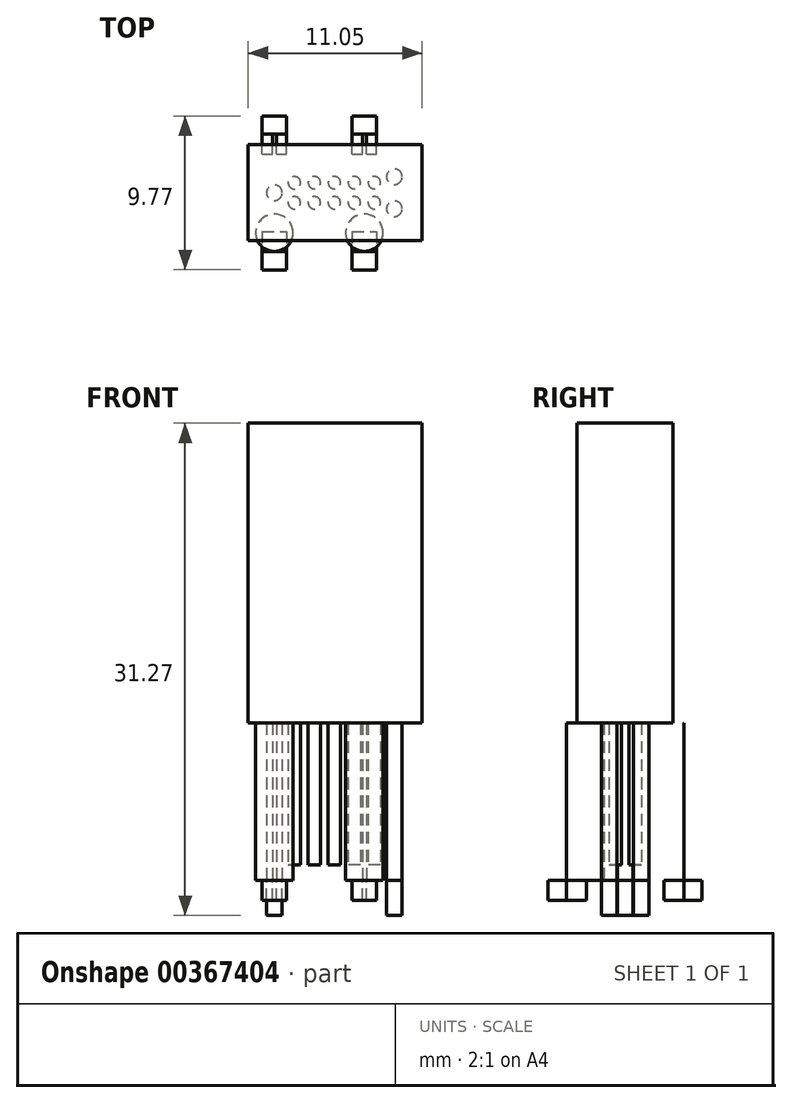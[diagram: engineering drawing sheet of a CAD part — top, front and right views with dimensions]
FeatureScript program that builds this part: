
annotation { "Feature Type Name" : "Feature", "Feature Type Description" : "" }
export const myFeature = defineFeature(function(context is Context, id is Id, definition is map)
    precondition{}
    {
        {
            var Q0;
            Q0=qCreatedBy(makeId("Top.planeOp"),FACE);
            var sketch = newSketch(context, id + "F0", { "sketchPlane" : qUnion([Q0])});
            skCircle(sketch, "E0", {"center": v(0, 0) * mm, "radius": 0.5 * mm});
            skCircle(sketch, "E1", {"center": v(7.62, -1.02) * mm, "radius": 0.5 * mm});
            skCircle(sketch, "E2", {"center": v(7.62, 1.02) * mm, "radius": 0.5 * mm});
            skCircle(sketch, "E3", {"center": v(1.27, 0.64) * mm, "radius": 0.4 * mm});
            skCircle(sketch, "E4", {"center": v(1.27, -0.63) * mm, "radius": 0.4 * mm});
            skCircle(sketch, "E5", {"center": v(2.54, 0.64) * mm, "radius": 0.4 * mm});
            skCircle(sketch, "E6", {"center": v(2.54, -0.63) * mm, "radius": 0.4 * mm});
            skCircle(sketch, "E7", {"center": v(3.81, 0.64) * mm, "radius": 0.4 * mm});
            skCircle(sketch, "E8", {"center": v(3.81, -0.63) * mm, "radius": 0.4 * mm});
            skCircle(sketch, "E9", {"center": v(0, 2.54) * mm, "radius": 1.19 * mm});
            skCircle(sketch, "E10", {"center": v(5.72, 2.54) * mm, "radius": 1.19 * mm});
            skCircle(sketch, "E11", {"center": v(0, -2.54) * mm, "radius": 1.19 * mm});
            skCircle(sketch, "E12", {"center": v(5.72, -2.54) * mm, "radius": 1.19 * mm});
            skLineSegment(sketch, "E13.bottom", {"start": v(-0.77, 4.88) * mm, "end": v(0.77, 4.88) * mm});
            skLineSegment(sketch, "E13.top", {"start": v(-0.77, 3.72) * mm, "end": v(0.77, 3.72) * mm});
            skLineSegment(sketch, "E13.left", {"start": v(-0.77, 4.88) * mm, "end": v(-0.77, 3.72) * mm});
            skLineSegment(sketch, "E13.right", {"start": v(0.77, 4.88) * mm, "end": v(0.77, 3.72) * mm});
            skLineSegment(sketch, "E14.bottom", {"start": v(4.94, 4.88) * mm, "end": v(6.49, 4.88) * mm});
            skLineSegment(sketch, "E14.top", {"start": v(4.94, 3.72) * mm, "end": v(6.49, 3.72) * mm});
            skLineSegment(sketch, "E14.left", {"start": v(4.94, 4.88) * mm, "end": v(4.94, 3.72) * mm});
            skLineSegment(sketch, "E14.right", {"start": v(6.49, 4.88) * mm, "end": v(6.49, 3.72) * mm});
            skLineSegment(sketch, "E15.bottom", {"start": v(-0.77, -3.73) * mm, "end": v(0.77, -3.73) * mm});
            skLineSegment(sketch, "E15.top", {"start": v(-0.77, -4.9) * mm, "end": v(0.77, -4.9) * mm});
            skLineSegment(sketch, "E15.left", {"start": v(-0.77, -3.73) * mm, "end": v(-0.77, -4.9) * mm});
            skLineSegment(sketch, "E15.right", {"start": v(0.77, -3.73) * mm, "end": v(0.77, -4.9) * mm});
            skLineSegment(sketch, "E16.bottom", {"start": v(4.94, -3.73) * mm, "end": v(6.49, -3.73) * mm});
            skLineSegment(sketch, "E16.top", {"start": v(4.94, -4.9) * mm, "end": v(6.49, -4.9) * mm});
            skLineSegment(sketch, "E16.left", {"start": v(4.94, -3.73) * mm, "end": v(4.94, -4.9) * mm});
            skLineSegment(sketch, "E16.right", {"start": v(6.49, -3.73) * mm, "end": v(6.49, -4.9) * mm});
            skCircle(sketch, "E17", {"center": v(5.08, 0.64) * mm, "radius": 0.4 * mm});
            skCircle(sketch, "E18", {"center": v(6.35, 0.64) * mm, "radius": 0.4 * mm});
            skCircle(sketch, "E19", {"center": v(6.35, -0.63) * mm, "radius": 0.4 * mm});
            skCircle(sketch, "E20", {"center": v(5.08, -0.63) * mm, "radius": 0.4 * mm});
            skSolve(sketch);
        }
        {
            var Q0;
            Q0=makeQuery(id+"F0.imprint","IMPRINT",FACE,{"disambiguationData":[TD([[makeQuery(id+"F0.imprint","IMPRINT",EDGE,{"derivedFrom":sQuery(id+"F0.wireOp",EDGE,"E13.bottom")}),-1.0]])]});
            var Q1;
            Q1=makeQuery(id+"F0.imprint","IMPRINT",FACE,{"disambiguationData":[TD([[makeQuery(id+"F0.imprint","IMPRINT",EDGE,{"derivedFrom":sQuery(id+"F0.wireOp",EDGE,"E14.bottom")}),-1.0]])]});
            var Q2;
            Q2=makeQuery(id+"F0.imprint","IMPRINT",FACE,{"disambiguationData":[TD([[makeQuery(id+"F0.imprint","IMPRINT",EDGE,{"derivedFrom":sQuery(id+"F0.wireOp",EDGE,"E15.bottom")}),-1.0]])]});
            var Q3;
            Q3=makeQuery(id+"F0.imprint","IMPRINT",FACE,{"disambiguationData":[TD([[makeQuery(id+"F0.imprint","IMPRINT",EDGE,{"derivedFrom":sQuery(id+"F0.wireOp",EDGE,"E16.bottom")}),-1.0]])]});
            extrude(context, id + "F1", {"entities" : qUnion([Q0, Q1, Q2, Q3]), "depth" : -1.27 * mm});
        }
        {
            var Q0;
            Q0=makeQuery(id+"F0.imprint","IMPRINT",FACE,{"disambiguationData":[TD([[makeQuery(id+"F0.imprint","IMPRINT",EDGE,{"derivedFrom":sQuery(id+"F0.wireOp",EDGE,"E1")}),1.0]])]});
            var Q1;
            Q1=makeQuery(id+"F0.imprint","IMPRINT",FACE,{"disambiguationData":[TD([[makeQuery(id+"F0.imprint","IMPRINT",EDGE,{"derivedFrom":sQuery(id+"F0.wireOp",EDGE,"E2")}),1.0]])]});
            var Q2;
            Q2=makeQuery(id+"F0.imprint","IMPRINT",FACE,{"disambiguationData":[TD([[makeQuery(id+"F0.imprint","IMPRINT",EDGE,{"derivedFrom":sQuery(id+"F0.wireOp",EDGE,"E0")}),1.0]])]});
            extrude(context, id + "F2", {"entities" : qUnion([Q0, Q1, Q2]), "depth" : -2.24 * mm});
        }
        {
            var Q0;
            Q0=makeQuery(id+"F0.imprint","IMPRINT",FACE,{"disambiguationData":[TD([[makeQuery(id+"F0.imprint","IMPRINT",EDGE,{"derivedFrom":sQuery(id+"F0.wireOp",EDGE,"E11")}),1.0]])]});
            var Q1;
            Q1=makeQuery(id+"F0.imprint","IMPRINT",FACE,{"disambiguationData":[TD([[makeQuery(id+"F0.imprint","IMPRINT",EDGE,{"derivedFrom":sQuery(id+"F0.wireOp",EDGE,"E12")}),1.0]])]});
            var Q2;
            {var subQ0=sQuery(id+"F0.wireOp",EDGE,"E14.top");var subQ1=sQuery(id+"F0.wireOp",EDGE,"E10");var subQ2=makeQuery(id+"F0.imprint","INTERSECT",VERTEX,{"disambiguationData":[OD(0.0)],"derivedFrom":[subQ1,subQ0]});Q2=makeQuery(id+"F0.imprint","IMPRINT",FACE,{"disambiguationData":[TD([[makeQuery(id+"F0.imprint","IMPRINT",EDGE,{"disambiguationData":[TD([[subQ2,-1.0]])],"derivedFrom":subQ1}),1.0]])]});}
            var Q3;
            {var subQ0=sQuery(id+"F0.wireOp",EDGE,"E13.top");var subQ1=sQuery(id+"F0.wireOp",EDGE,"E9");var subQ2=makeQuery(id+"F0.imprint","INTERSECT",VERTEX,{"disambiguationData":[OD(0.0)],"derivedFrom":[subQ1,subQ0]});Q3=makeQuery(id+"F0.imprint","IMPRINT",FACE,{"disambiguationData":[TD([[makeQuery(id+"F0.imprint","IMPRINT",EDGE,{"disambiguationData":[TD([[subQ2,-1.0]])],"derivedFrom":subQ1}),1.0]])]});}
            extrude(context, id + "F3", {"entities" : qUnion([Q0, Q1, Q2, Q3]), "depth" : 9.98 * mm});
        }
        {
            var Q0;
            {var subQ0=sQuery(id+"F0.wireOp",EDGE,"E13.top");Q0=makeQuery(id+"F1.opExtrude","SWEPT_FACE",FACE,{"disambiguationData":[OSD([subQ0]),TDD([makeQuery(id+"F0.imprint","IMPRINT",EDGE,{"disambiguationData":[TD([[makeQuery(id+"F0.imprint","INTERSECT",VERTEX,{"derivedFrom":[subQ0,sQuery(id+"F0.wireOp",EDGE,"E13.right")]}),1.0]])],"derivedFrom":subQ0})])]});}
            var Q1;
            {var subQ0=sQuery(id+"F0.wireOp",EDGE,"E13.top");Q1=makeQuery(id+"F1.opExtrude","SWEPT_FACE",FACE,{"disambiguationData":[OSD([subQ0]),TDD([makeQuery(id+"F0.imprint","IMPRINT",EDGE,{"disambiguationData":[TD([[makeQuery(id+"F0.imprint","INTERSECT",VERTEX,{"derivedFrom":[subQ0,sQuery(id+"F0.wireOp",EDGE,"E13.left")]}),-1.0]])],"derivedFrom":subQ0})])]});}
            var Q2;
            {var subQ0=sQuery(id+"F0.wireOp",EDGE,"E14.top");Q2=makeQuery(id+"F1.opExtrude","SWEPT_FACE",FACE,{"disambiguationData":[OSD([subQ0]),TDD([makeQuery(id+"F0.imprint","IMPRINT",EDGE,{"disambiguationData":[TD([[makeQuery(id+"F0.imprint","INTERSECT",VERTEX,{"derivedFrom":[subQ0,sQuery(id+"F0.wireOp",EDGE,"E14.left")]}),-1.0]])],"derivedFrom":subQ0})])]});}
            var Q3;
            {var subQ0=sQuery(id+"F0.wireOp",EDGE,"E14.top");Q3=makeQuery(id+"F1.opExtrude","SWEPT_FACE",FACE,{"disambiguationData":[OSD([subQ0]),TDD([makeQuery(id+"F0.imprint","IMPRINT",EDGE,{"disambiguationData":[TD([[makeQuery(id+"F0.imprint","INTERSECT",VERTEX,{"derivedFrom":[subQ0,sQuery(id+"F0.wireOp",EDGE,"E14.right")]}),1.0]])],"derivedFrom":subQ0})])]});}
            extrude(context, id + "F4", {"entities" : qUnion([Q0, Q1, Q2, Q3]), "depth" : 1.27 * mm});
        }
        {
            var Q0;
            Q0=makeQuery(id+"F1.opExtrude","SWEPT_FACE",FACE,{"disambiguationData":[OSD([sQuery(id+"F0.wireOp",EDGE,"E15.bottom")])]});
            var Q1;
            Q1=makeQuery(id+"F1.opExtrude","SWEPT_FACE",FACE,{"disambiguationData":[OSD([sQuery(id+"F0.wireOp",EDGE,"E16.bottom")])]});
            extrude(context, id + "F5", {"entities" : qUnion([Q0, Q1]), "depth" : 1.27 * mm});
        }
        {
            var Q0;
            Q0=makeQuery(id+"F0.imprint","IMPRINT",FACE,{"disambiguationData":[TD([[makeQuery(id+"F0.imprint","IMPRINT",EDGE,{"derivedFrom":sQuery(id+"F0.wireOp",EDGE,"E8")}),1.0]])]});
            var Q1;
            Q1=makeQuery(id+"F0.imprint","IMPRINT",FACE,{"disambiguationData":[TD([[makeQuery(id+"F0.imprint","IMPRINT",EDGE,{"derivedFrom":sQuery(id+"F0.wireOp",EDGE,"E7")}),1.0]])]});
            var Q2;
            Q2=makeQuery(id+"F0.imprint","IMPRINT",FACE,{"disambiguationData":[TD([[makeQuery(id+"F0.imprint","IMPRINT",EDGE,{"derivedFrom":sQuery(id+"F0.wireOp",EDGE,"E5")}),1.0]])]});
            var Q3;
            Q3=makeQuery(id+"F0.imprint","IMPRINT",FACE,{"disambiguationData":[TD([[makeQuery(id+"F0.imprint","IMPRINT",EDGE,{"derivedFrom":sQuery(id+"F0.wireOp",EDGE,"E6")}),1.0]])]});
            var Q4;
            Q4=makeQuery(id+"F0.imprint","IMPRINT",FACE,{"disambiguationData":[TD([[makeQuery(id+"F0.imprint","IMPRINT",EDGE,{"derivedFrom":sQuery(id+"F0.wireOp",EDGE,"E4")}),1.0]])]});
            var Q5;
            Q5=makeQuery(id+"F0.imprint","IMPRINT",FACE,{"disambiguationData":[TD([[makeQuery(id+"F0.imprint","IMPRINT",EDGE,{"derivedFrom":sQuery(id+"F0.wireOp",EDGE,"E3")}),1.0]])]});
            var Q6;
            Q6=makeQuery(id+"F0.imprint","IMPRINT",FACE,{"disambiguationData":[TD([[makeQuery(id+"F0.imprint","IMPRINT",EDGE,{"derivedFrom":sQuery(id+"F0.wireOp",EDGE,"E20")}),1.0]])]});
            var Q7;
            Q7=makeQuery(id+"F0.imprint","IMPRINT",FACE,{"disambiguationData":[TD([[makeQuery(id+"F0.imprint","IMPRINT",EDGE,{"derivedFrom":sQuery(id+"F0.wireOp",EDGE,"E17")}),1.0]])]});
            var Q8;
            Q8=makeQuery(id+"F0.imprint","IMPRINT",FACE,{"disambiguationData":[TD([[makeQuery(id+"F0.imprint","IMPRINT",EDGE,{"derivedFrom":sQuery(id+"F0.wireOp",EDGE,"E18")}),1.0]])]});
            var Q9;
            Q9=makeQuery(id+"F0.imprint","IMPRINT",FACE,{"disambiguationData":[TD([[makeQuery(id+"F0.imprint","IMPRINT",EDGE,{"derivedFrom":sQuery(id+"F0.wireOp",EDGE,"E19")}),1.0]])]});
            extrude(context, id + "F6", {"entities" : qUnion([Q0, Q1, Q2, Q3, Q4, Q5, Q6, Q7, Q8, Q9]), "depth" : 9.98 * mm, "hasSecondDirection" : true, "secondDirectionOppositeDirection" : true, "secondDirectionDepth" : -1 * mm});
        }
        {
            var Q0;
            Q0=makeQuery(id+"F3.opExtrude","CAP_FACE",FACE,{"disambiguationData":[OSD([sQuery(id+"F0.wireOp",EDGE,"E9"),sQuery(id+"F0.wireOp",EDGE,"E13.top")])],"isStart":false});
            var sketch = newSketch(context, id + "F7", { "sketchPlane" : qUnion([Q0])});
            skLineSegment(sketch, "E21.bottom", {"start": v(9.4, 3.05) * mm, "end": v(-1.66, 3.05) * mm});
            skLineSegment(sketch, "E21.top", {"start": v(9.4, -3.05) * mm, "end": v(-1.66, -3.05) * mm});
            skLineSegment(sketch, "E21.left", {"start": v(9.4, 3.05) * mm, "end": v(9.4, -3.05) * mm});
            skLineSegment(sketch, "E21.right", {"start": v(-1.66, 3.05) * mm, "end": v(-1.66, -3.05) * mm});
            skSolve(sketch);
        }
        {
            var Q0;
            Q0=makeQuery(id+"F7.imprint","IMPRINT",FACE,{"disambiguationData":[TD([[makeQuery(id+"F7.imprint","IMPRINT",EDGE,{"derivedFrom":sQuery(id+"F7.wireOp",EDGE,"E21.top")}),-1.0]])]});
            var Q1;
            {var subQ0=sQuery(id+"F7.wireOp",EDGE,"E21.bottom");var subQ1=makeQuery(id+"F3.opExtrude","CAP_EDGE",EDGE,{"disambiguationData":[OSD([sQuery(id+"F0.wireOp",EDGE,"E9")])],"isStart":false});var subQ2=makeQuery(id+"F7.imprint","INTERSECT",VERTEX,{"disambiguationData":[OD(0.0)],"derivedFrom":[subQ1,subQ0]});Q1=makeQuery(id+"F7.imprint","IMPRINT",FACE,{"disambiguationData":[TD([[makeQuery(id+"F7.imprint","IMPRINT",EDGE,{"disambiguationData":[TD([[subQ2,-1.0]])],"derivedFrom":subQ0}),1.0]])]});}
            extrude(context, id + "F8", {"entities" : qUnion([Q0, Q1]), "depth" : 19.05 * mm});
        }
        {
            var Q0;
            Q0=makeQuery(id+"F0.imprint","IMPRINT",FACE,{"disambiguationData":[TD([[makeQuery(id+"F0.imprint","IMPRINT",EDGE,{"derivedFrom":sQuery(id+"F0.wireOp",EDGE,"E2")}),1.0]])]});
            var Q1;
            Q1=makeQuery(id+"F0.imprint","IMPRINT",FACE,{"disambiguationData":[TD([[makeQuery(id+"F0.imprint","IMPRINT",EDGE,{"derivedFrom":sQuery(id+"F0.wireOp",EDGE,"E1")}),1.0]])]});
            var Q2;
            Q2=makeQuery(id+"F0.imprint","IMPRINT",FACE,{"disambiguationData":[TD([[makeQuery(id+"F0.imprint","IMPRINT",EDGE,{"derivedFrom":sQuery(id+"F0.wireOp",EDGE,"E0")}),1.0]])]});
            extrude(context, id + "F9", {"entities" : qUnion([Q0, Q1, Q2]), "depth" : 9.98 * mm});
        }
    });
